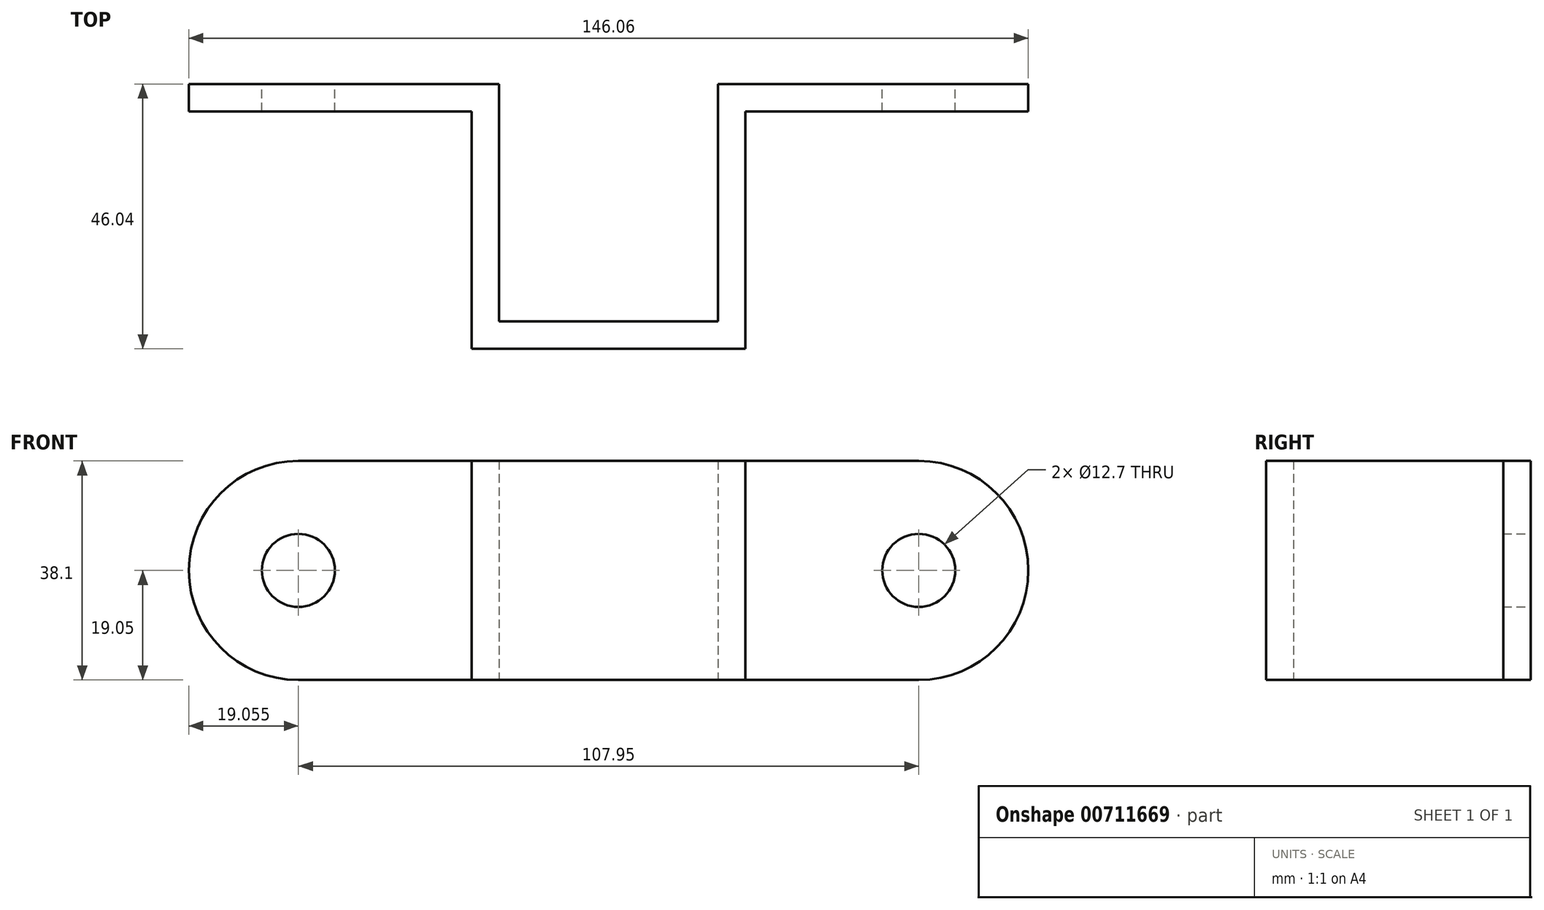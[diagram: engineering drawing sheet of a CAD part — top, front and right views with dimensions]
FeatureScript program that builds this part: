
annotation { "Feature Type Name" : "Feature", "Feature Type Description" : "" }
export const myFeature = defineFeature(function(context is Context, id is Id, definition is map)
    precondition{}
    {
        {
            var Q0;
            Q0=qCreatedBy(makeId("Top.planeOp"),FACE);
            var sketch = newSketch(context, id + "F0", { "sketchPlane" : qUnion([Q0])});
            skLineSegment(sketch, "E0", {"start": v(-19.05, 0) * mm, "end": v(-53.98, 0) * mm});
            skLineSegment(sketch, "E1", {"start": v(-19.05, 0) * mm, "end": v(-19.05, -41.28) * mm});
            skLineSegment(sketch, "E2", {"start": v(-19.05, -41.28) * mm, "end": v(19.05, -41.28) * mm});
            skLineSegment(sketch, "E3", {"start": v(19.05, -41.28) * mm, "end": v(19.05, 0) * mm});
            skLineSegment(sketch, "E4", {"start": v(19.05, 0) * mm, "end": v(53.98, 0) * mm});
            skLineSegment(sketch, "E5", {"start": v(53.98, -4.76) * mm, "end": v(23.81, -4.76) * mm});
            skLineSegment(sketch, "E6.0", {"start": v(-23.81, -4.76) * mm, "end": v(-23.81, -46.04) * mm});
            skLineSegment(sketch, "E7.0", {"start": v(23.81, -46.04) * mm, "end": v(23.81, -4.76) * mm});
            skLineSegment(sketch, "E8.0", {"start": v(-23.81, -46.04) * mm, "end": v(24.44, -46.04) * mm});
            skLineSegment(sketch, "E9.trimOffspring", {"start": v(-23.81, -4.76) * mm, "end": v(-53.98, -4.76) * mm});
            skLineSegment(sketch, "E10", {"start": v(-53.98, 0) * mm, "end": v(-53.98, -4.76) * mm});
            skLineSegment(sketch, "E11", {"start": v(53.98, 0) * mm, "end": v(53.98, -4.76) * mm});
            skSolve(sketch);
        }
        {
            var Q0;
            Q0=makeQuery(id+"F0.imprint","IMPRINT",FACE,{"disambiguationData":[TD([[makeQuery(id+"F0.imprint","IMPRINT",EDGE,{"derivedFrom":sQuery(id+"F0.wireOp",EDGE,"E0")}),1.0]])]});
            extrude(context, id + "F1", {"entities" : qUnion([Q0]), "depth" : 19.05 * mm, "offsetDistance" : 25.4 * mm, "hasSecondDirection" : true, "secondDirectionOppositeDirection" : true, "secondDirectionDepth" : 19.05 * mm});
        }
        {
            var Q0;
            Q0=qCreatedBy(makeId("Front.planeOp"),FACE);
            var sketch = newSketch(context, id + "F2", { "sketchPlane" : qUnion([Q0])});
            skPoint(sketch, "E12.0", {"position": v(-53.98, 0) * mm});
            skPoint(sketch, "E13.0", {"position": v(53.98, 0) * mm});
            skCircle(sketch, "E14", {"center": v(-53.98, 0) * mm, "radius": 6.35 * mm});
            skCircle(sketch, "E15", {"center": v(53.98, 0) * mm, "radius": 6.35 * mm});
            skCircle(sketch, "E16", {"center": v(53.98, 0) * mm, "radius": 19.05 * mm});
            skCircle(sketch, "E17", {"center": v(-53.98, 0) * mm, "radius": 19.05 * mm});
            skSolve(sketch);
        }
        {
            var Q0;
            Q0=sQuery(id+"F2.wireOp",VERTEX,"E12.0");
            var Q1;
            Q1=sQuery(id+"F2.wireOp",VERTEX,"E13.0");
            var Q2;
            Q2=makeQuery(id+"F1.opExtrude","SWEPT_BODY",BODY,{"disambiguationData":[OSD([sQuery(id+"F0.wireOp",EDGE,"E0"),sQuery(id+"F0.wireOp",EDGE,"E1"),sQuery(id+"F0.wireOp",EDGE,"E2"),sQuery(id+"F0.wireOp",EDGE,"E3"),sQuery(id+"F0.wireOp",EDGE,"E4"),sQuery(id+"F0.wireOp",EDGE,"E5"),sQuery(id+"F0.wireOp",EDGE,"E6.0"),sQuery(id+"F0.wireOp",EDGE,"E7.0"),sQuery(id+"F0.wireOp",EDGE,"E8.0"),sQuery(id+"F0.wireOp",EDGE,"E9.trimOffspring"),sQuery(id+"F0.wireOp",EDGE,"E10"),sQuery(id+"F0.wireOp",EDGE,"E11")])]});
            hole(context, id + "F3", {"style" : HoleStyle.SIMPLE, "endStyle" : HoleEndStyle.THROUGH, "oppositeDirection" : true, "holeDiameter" : 12.7 * mm, "majorDiameter" : 6.35 * mm, "isTappedThrough" : true, "tappedDepth" : 12.7 * mm, "tapClearance" : 3, "locations" : qUnion([Q0, Q1]), "scope" : qUnion([Q2])});
        }
        {
            var Q0;
            Q0=makeQuery(id+"F2.imprint","IMPRINT",FACE,{"disambiguationData":[TD([[makeQuery(id+"F2.imprint","IMPRINT",EDGE,{"derivedFrom":sQuery(id+"F2.wireOp",EDGE,"E14")}),-1.0]])]});
            var Q1;
            Q1=makeQuery(id+"F2.imprint","IMPRINT",FACE,{"disambiguationData":[TD([[makeQuery(id+"F2.imprint","IMPRINT",EDGE,{"derivedFrom":sQuery(id+"F2.wireOp",EDGE,"E15")}),-1.0]])]});
            extrude(context, id + "F4", {"entities" : qUnion([Q0, Q1]), "operationType" : NewBodyOperationType.ADD, "depth" : 4.76 * mm, "offsetDistance" : 25.4 * mm});
        }
    });
